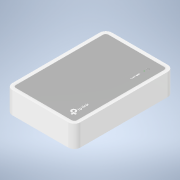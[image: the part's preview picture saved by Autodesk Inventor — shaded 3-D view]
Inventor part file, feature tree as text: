
AUTODESK INVENTOR PART (.ipt)
format: ipt  version: 2020.1 (Build 241239000, 239)  size: 997,888 bytes
history: native  units: in
note: dims shown in document units (in); Inventor stores cm internally (conversion verified against a paired STEP export)
features: projected_geometry x18, sketch x15, extrude x9, other x6, sweep x1, fillet x1
ambient origin geometry x8: Origin, YZ Plane, XZ Plane, XY Plane, X Axis, Y Axis, Z Axis, Center Point
bodies: Solid1 (feature_tree)
feature tree (50):
  extrude  "Extrusion1"  Depth=4.1in
  extrude  "Extrusion2"  Depth=0.469in
  extrude  "Extrusion3"  Depth=0.0155in
  sweep  "Sweep1"
  extrude  "Extrusion4"  Depth=0.1105in
  fillet  "Fillet1"  Radius=0.0356in
  extrude  "Extrusion5"  Depth=0.045in
  extrude  "Extrusion6"  Depth=0.05in
  other  "Decal1"
  extrude  "Extrusion7"  Depth=0.25in
  extrude  "Extrusion8"  Depth=4.1in
  other  "Decal2"
  sketch  "Sketch17"  dims[d27=0.0645in]
  other  "Decal3"
  extrude  "Extrusion9"  Depth=0.9in
  sketch  "Sketch1"  dims[d0=2.8in d1=4.1in]
  sketch  "Sketch2"  dims[d2=0.9in d3=0.0in d4=0.469in]
  projected_geometry  "Projected Loop1"
  sketch  "Sketch3"  dims[d5=0.079in d6=0.0155in]
  sketch  "Sketch5"  dims[d7=0.11in d8=0.0155in]
  sketch  "Sketch7"  dims[d9=0.08in d10=0.1105in d11=0.0356in]
  sketch  "Sketch8"  dims[d12=0.044in d13=0.045in]
  sketch  "Sketch9"  dims[d14=0.16in d15=0.05in]
  projected_geometry  "Projected Loop2"
  projected_geometry  "Projected Loop3"
  projected_geometry  "Projected Loop4"
  projected_geometry  "Projected Loop5"
  projected_geometry  "Projected Loop6"
  projected_geometry  "Projected Loop7"
  projected_geometry  "Projected Loop8"
  projected_geometry  "Projected Loop9"
  projected_geometry  "Projected Loop10"
  projected_geometry  "Projected Loop11"
  projected_geometry  "Projected Loop12"
  projected_geometry  "Projected Loop13"
  projected_geometry  "Projected Loop14"
  projected_geometry  "Projected Loop15"
  projected_geometry  "Projected Loop16"
  sketch  "Sketch10"  dims[d16=0.25in d18=0.25in]
  projected_geometry  "Projected Loop17"
  sketch  "Sketch11"  dims[d19=2.8in d20=4.1in]
  other  "Image1"
  sketch  "Sketch12"  dims[d21=0.65in d22=0.9in]
  projected_geometry  "Projected Loop18"
  sketch  "Sketch13"  dims[d23=0.3496in]
  sketch  "Sketch15"  dims[d25=0.443in d26=0.0in]
  other  "Image4"
  sketch  "Sketch18"  dims[d28=0.025in]
  other  "Image5"
  sketch  "Sketch20"  dims[d29=0.25in d31=0.025in d32=0.25in d33=0.16in d34=0.08in d35=0.119in d36=0.0in d37=0.0185in d38=0.0374in d39=0.0107in d40=0.0107in d41=0.1257in d42=0.1464in d43=0.8012in d48=0.0093in d49=0.0187in d50=0.1443in d51=0.0in d52=0.0in d53=0.02in d54=0.02in d55=0.02in d56=0.02in d57=0.02in d58=0.005in d59=0.0in d60=0.25in d61=0.079in d62=0.025in d63=0.025in d65=0.002in d66=0.0in d67=0.15in d68=0.001in d69=0.0in d71=0.75in d94=0.1376in d95=0.01in d96=0.1in d97=0.0in d98=0.025in d99=0.025in d100=0.025in d101=0.0001in d102=0.0in d103=0.0in d104=0.0001in d261=0.04in d262=0.002in d263=0.0in]
